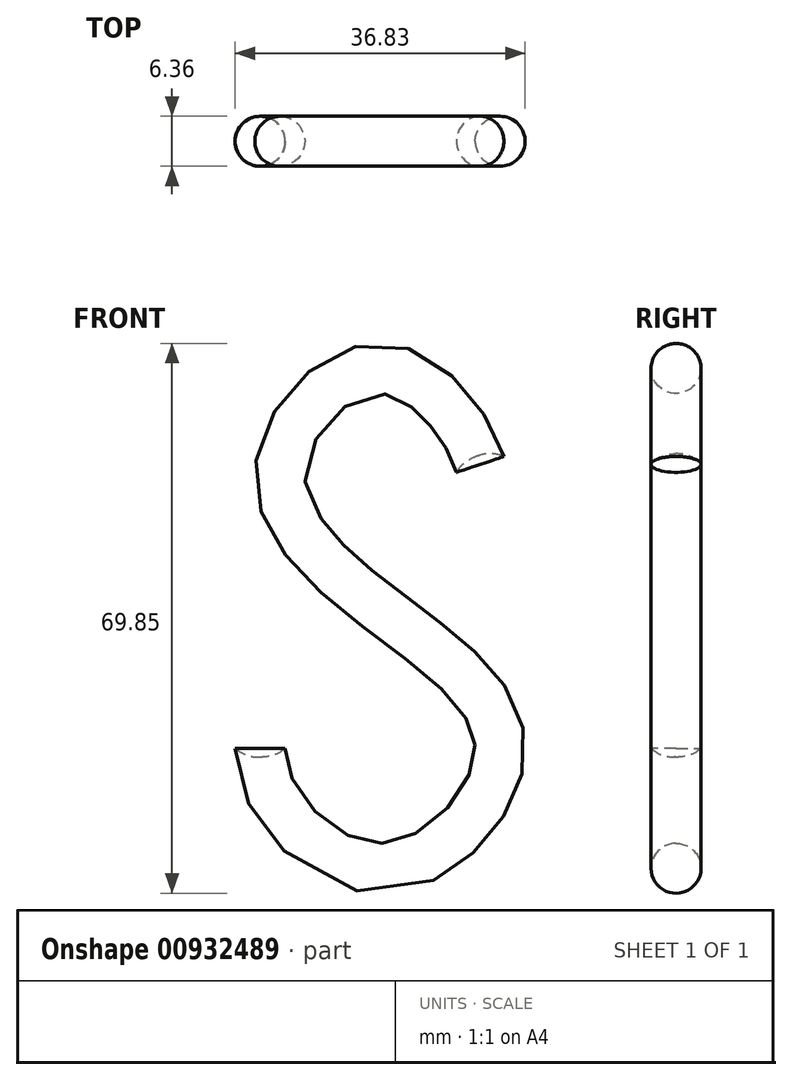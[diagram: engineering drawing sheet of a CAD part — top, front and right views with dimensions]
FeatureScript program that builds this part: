
annotation { "Feature Type Name" : "Feature", "Feature Type Description" : "" }
export const myFeature = defineFeature(function(context is Context, id is Id, definition is map)
    precondition{}
    {
        {
            var Q0;
            Q0=qCreatedBy(makeId("Front.planeOp"),FACE);
            var sketch = newSketch(context, id + "F0", { "sketchPlane" : qUnion([Q0])});
            skFitSpline(sketch, "E0", {"points": [v(12.7, 18.29) * mm, v(0, 30.48) * mm, v(-12.7, 17.78) * mm, v(0, 0) * mm, v(15.24, -17.78) * mm, v(0, -33.02) * mm, v(-15.24, -17.78) * mm], "startDerivative": vector(-29.2, 98.91) * mm, "endDerivative": vector(4.3, 118.4) * mm});
            skLineSegment(sketch, "E1", {"start": v(-15.24, -17.78) * mm, "end": v(-15.24, -12.47) * mm, "construction": true});
            skSolve(sketch);
        }
        {
            var Q0;
            Q0=sQuery(id+"F0.wireOp",VERTEX,"E0.end");
            var Q1;
            Q1=sQuery(id+"F0.wireOp",EDGE,"E1");
            cPlane(context, id + "F1", {"entities" : qUnion([Q0, Q1]), "cplaneType" : CPlaneType.LINE_POINT, "offset" : 25.4 * mm, "width" : 152.4 * mm, "height" : 152.4 * mm});
        }
        {
            var Q0;
            Q0=qCreatedBy(id+"F1.planeOp",FACE);
            var sketch = newSketch(context, id + "F2", { "sketchPlane" : qUnion([Q0])});
            skCircle(sketch, "E2", {"center": v(-15.24, 0) * mm, "radius": 3.18 * mm});
            skSolve(sketch);
        }
        {
            var Q0;
            Q0=makeQuery(id+"F2.imprint","IMPRINT",FACE,{"disambiguationData":[TD([[makeQuery(id+"F2.imprint","IMPRINT",EDGE,{"derivedFrom":sQuery(id+"F2.wireOp",EDGE,"E2")}),1.0]])]});
            var Q1;
            Q1=sQuery(id+"F0.wireOp",EDGE,"E0");
            sweep(context, id + "F3", {"profiles" : qUnion([Q0]), "path" : qUnion([Q1])});
        }
        {
            var Q0;
            Q0=makeQuery(id+"F3.opSweep","CAP_FACE",FACE,{"disambiguationData":[OSD([sQuery(id+"F0.wireOp",VERTEX,"E0.start"),sQuery(id+"F2.wireOp",EDGE,"E2")])],"isStart":false});
            cPlane(context, id + "F4", {"entities" : qUnion([Q0]), "cplaneType" : CPlaneType.OFFSET, "offset" : 0 * mm, "width" : 152.4 * mm, "height" : 152.4 * mm});
        }
        {
            var Q0;
            Q0=qCreatedBy(id+"F4.planeOp",FACE);
            var sketch = newSketch(context, id + "F5", { "sketchPlane" : qUnion([Q0])});
            skCircle(sketch, "E3.0", {"center": v(17.85, 0) * mm, "radius": 3.18 * mm});
            skSolve(sketch);
        }
        {
            var Q0;
            Q0=qCreatedBy(makeId("Front.planeOp"),FACE);
            var sketch = newSketch(context, id + "F6", { "sketchPlane" : qUnion([Q0])});
            skLineSegment(sketch, "E4", {"start": v(12.7, 18.29) * mm, "end": v(15.09, 11.16) * mm});
            skArc(sketch, "E5", {"start": v(15.09, 11.16) * mm, "mid": v(18.3, 15) * mm, "end": v(15.71, 19.3) * mm});
            skLineSegment(sketch, "E6", {"start": v(15.71, 19.3) * mm, "end": v(12.7, 18.29) * mm});
            skLineSegment(sketch, "E7", {"start": v(-15.24, -17.78) * mm, "end": v(-15.24, -10.26) * mm});
            skArc(sketch, "E8", {"start": v(-12.06, -17.78) * mm, "mid": v(-10.98, -12.9) * mm, "end": v(-15.24, -10.26) * mm});
            skLineSegment(sketch, "E9", {"start": v(-12.06, -17.78) * mm, "end": v(-15.24, -17.78) * mm});
            skSolve(sketch);
        }
        {
            var Q0;
            Q0=makeQuery(id+"F6.imprint","IMPRINT",FACE,{"disambiguationData":[TD([[makeQuery(id+"F6.imprint","IMPRINT",EDGE,{"derivedFrom":sQuery(id+"F6.wireOp",EDGE,"E4")}),1.0]])]});
            var Q1;
            Q1=sQuery(id+"F6.wireOp",EDGE,"E4");
            revolve(context, id + "F7", {"operationType" : NewBodyOperationType.ADD, "surfaceOperationType" : NewSurfaceOperationType.NEW, "entities" : qUnion([Q0]), "axis" : qUnion([Q1]), "revolveType" : RevolveType.FULL});
        }
        {
            var Q0;
            Q0=makeQuery(id+"F6.imprint","IMPRINT",FACE,{"disambiguationData":[TD([[makeQuery(id+"F6.imprint","IMPRINT",EDGE,{"derivedFrom":sQuery(id+"F6.wireOp",EDGE,"E7")}),-1.0]])]});
            var Q1;
            Q1=sQuery(id+"F6.wireOp",EDGE,"E7");
            revolve(context, id + "F8", {"operationType" : NewBodyOperationType.ADD, "surfaceOperationType" : NewSurfaceOperationType.NEW, "entities" : qUnion([Q0]), "axis" : qUnion([Q1]), "revolveType" : RevolveType.FULL});
        }
    });
